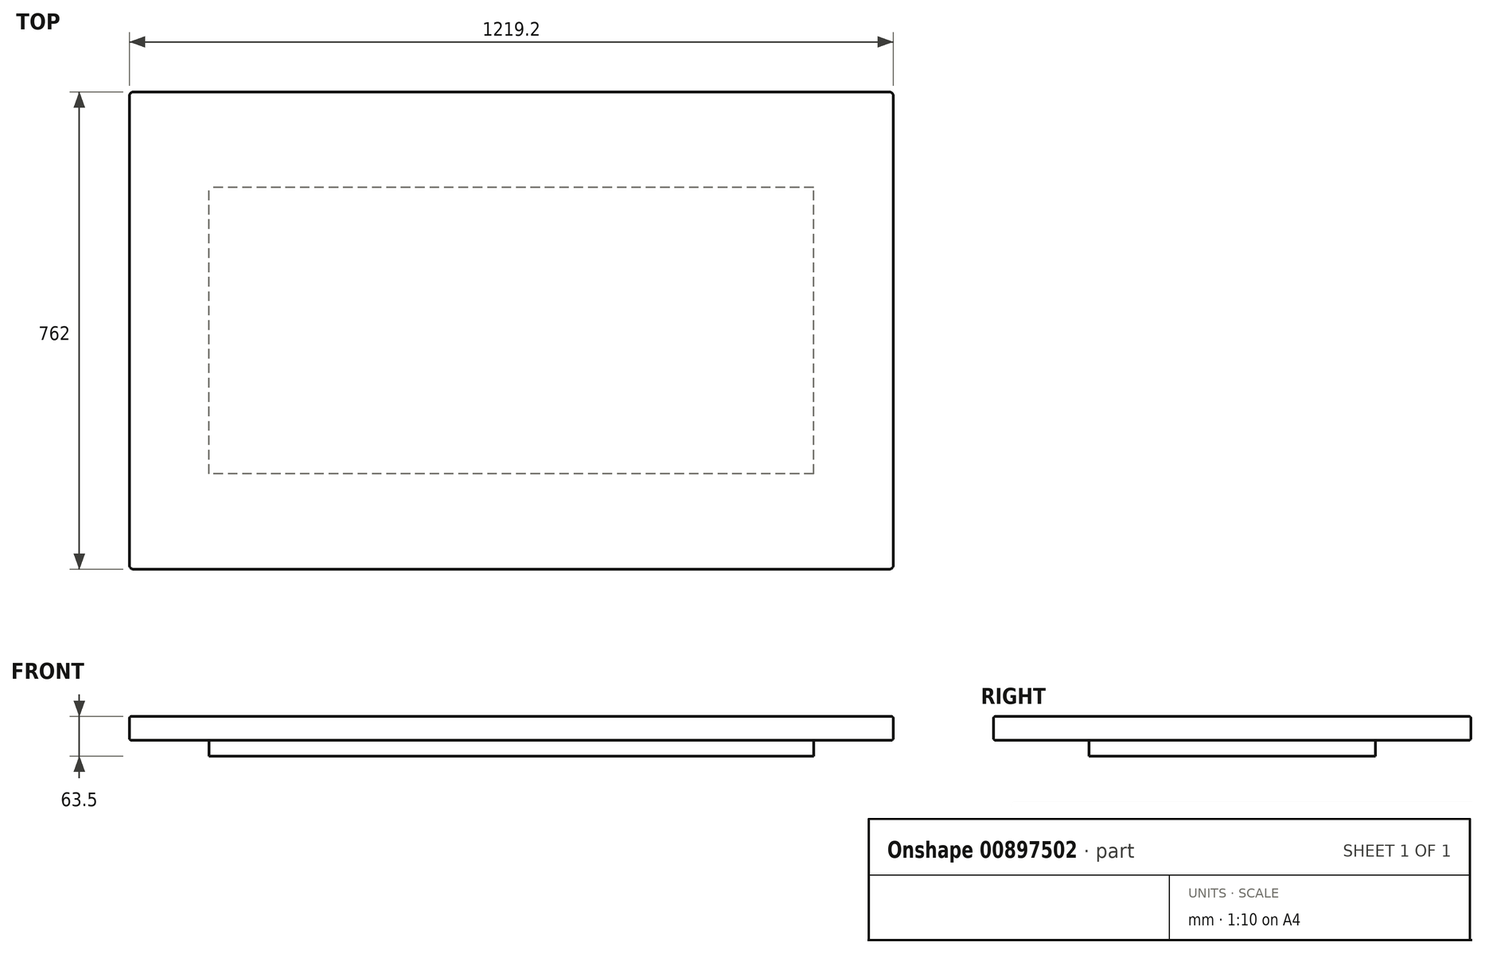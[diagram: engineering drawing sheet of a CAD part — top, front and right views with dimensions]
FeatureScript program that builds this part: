
annotation { "Feature Type Name" : "Feature", "Feature Type Description" : "" }
export const myFeature = defineFeature(function(context is Context, id is Id, definition is map)
    precondition{}
    {
        {
            var Q0;
            Q0=qCreatedBy(makeId("Top.planeOp"),FACE);
            var sketch = newSketch(context, id + "F0", { "sketchPlane" : qUnion([Q0])});
            skLineSegment(sketch, "E0.bottom", {"start": v(609.6, 381) * mm, "end": v(-609.6, 381) * mm});
            skLineSegment(sketch, "E0.top", {"start": v(609.6, -381) * mm, "end": v(-609.6, -381) * mm});
            skLineSegment(sketch, "E0.left", {"start": v(609.6, 381) * mm, "end": v(609.6, -381) * mm});
            skLineSegment(sketch, "E0.right", {"start": v(-609.6, 381) * mm, "end": v(-609.6, -381) * mm});
            skPoint(sketch, "E0.middle", {"position": v(0, 0) * mm});
            skSolve(sketch);
        }
        {
            var Q0;
            Q0=makeQuery(id+"F0.imprint","IMPRINT",FACE,{"disambiguationData":[TD([[makeQuery(id+"F0.imprint","IMPRINT",EDGE,{"derivedFrom":sQuery(id+"F0.wireOp",EDGE,"E0.bottom")}),1.0]])]});
            extrude(context, id + "F1", {"entities" : qUnion([Q0]), "depth" : 38.1 * mm, "offsetDistance" : 25.4 * mm});
        }
        {
            var Q0;
            Q0=makeQuery(id+"F1.opExtrude","SWEPT_EDGE",EDGE,{"disambiguationData":[OSD([sQuery(id+"F0.wireOp",EDGE,"E0.top"),sQuery(id+"F0.wireOp",EDGE,"E0.right")])]});
            var Q1;
            Q1=makeQuery(id+"F1.opExtrude","SWEPT_EDGE",EDGE,{"disambiguationData":[OSD([sQuery(id+"F0.wireOp",EDGE,"E0.top"),sQuery(id+"F0.wireOp",EDGE,"E0.left")])]});
            var Q2;
            Q2=makeQuery(id+"F1.opExtrude","SWEPT_EDGE",EDGE,{"disambiguationData":[OSD([sQuery(id+"F0.wireOp",EDGE,"E0.bottom"),sQuery(id+"F0.wireOp",EDGE,"E0.right")])]});
            var Q3;
            Q3=makeQuery(id+"F1.opExtrude","SWEPT_EDGE",EDGE,{"disambiguationData":[OSD([sQuery(id+"F0.wireOp",EDGE,"E0.bottom"),sQuery(id+"F0.wireOp",EDGE,"E0.left")])]});
            fillet(context, id + "F2", {"entities" : qUnion([Q0, Q1, Q2, Q3]), "radius" : 6.35 * mm, "tangentPropagation" : true, "allowEdgeOverflow" : false});
        }
        {
            var Q0;
            Q0=makeQuery(id+"F1.opExtrude","CAP_EDGE",EDGE,{"disambiguationData":[OSD([sQuery(id+"F0.wireOp",EDGE,"E0.left")])],"isStart":false});
            var Q1;
            Q1=makeQuery(id+"F1.opExtrude","CAP_EDGE",EDGE,{"disambiguationData":[OSD([sQuery(id+"F0.wireOp",EDGE,"E0.left")])],"isStart":true});
            fillet(context, id + "F3", {"entities" : qUnion([Q0, Q1]), "radius" : 3.17 * mm, "tangentPropagation" : true, "allowEdgeOverflow" : false});
        }
        {
            var Q0;
            Q0=makeQuery(id+"F1.opExtrude","CAP_FACE",FACE,{"disambiguationData":[OSD([sQuery(id+"F0.wireOp",EDGE,"E0.bottom"),sQuery(id+"F0.wireOp",EDGE,"E0.top"),sQuery(id+"F0.wireOp",EDGE,"E0.left"),sQuery(id+"F0.wireOp",EDGE,"E0.right")])],"isStart":true});
            var sketch = newSketch(context, id + "F4", { "sketchPlane" : qUnion([Q0])});
            skLineSegment(sketch, "E1.bottom", {"start": v(482.6, 228.6) * mm, "end": v(-482.6, 228.6) * mm});
            skLineSegment(sketch, "E1.top", {"start": v(482.6, -228.6) * mm, "end": v(-482.6, -228.6) * mm});
            skLineSegment(sketch, "E1.left", {"start": v(482.6, 228.6) * mm, "end": v(482.6, -228.6) * mm});
            skLineSegment(sketch, "E1.right", {"start": v(-482.6, 228.6) * mm, "end": v(-482.6, -228.6) * mm});
            skPoint(sketch, "E1.middle", {"position": v(0, 0) * mm});
            skSolve(sketch);
        }
        {
            var Q0;
            Q0=makeQuery(id+"F4.imprint","IMPRINT",FACE,{"disambiguationData":[TD([[makeQuery(id+"F4.imprint","IMPRINT",EDGE,{"derivedFrom":sQuery(id+"F4.wireOp",EDGE,"E1.bottom")}),1.0]])]});
            extrude(context, id + "F5", {"entities" : qUnion([Q0]), "depth" : 25.4 * mm, "offsetDistance" : 25.4 * mm});
        }
    });
